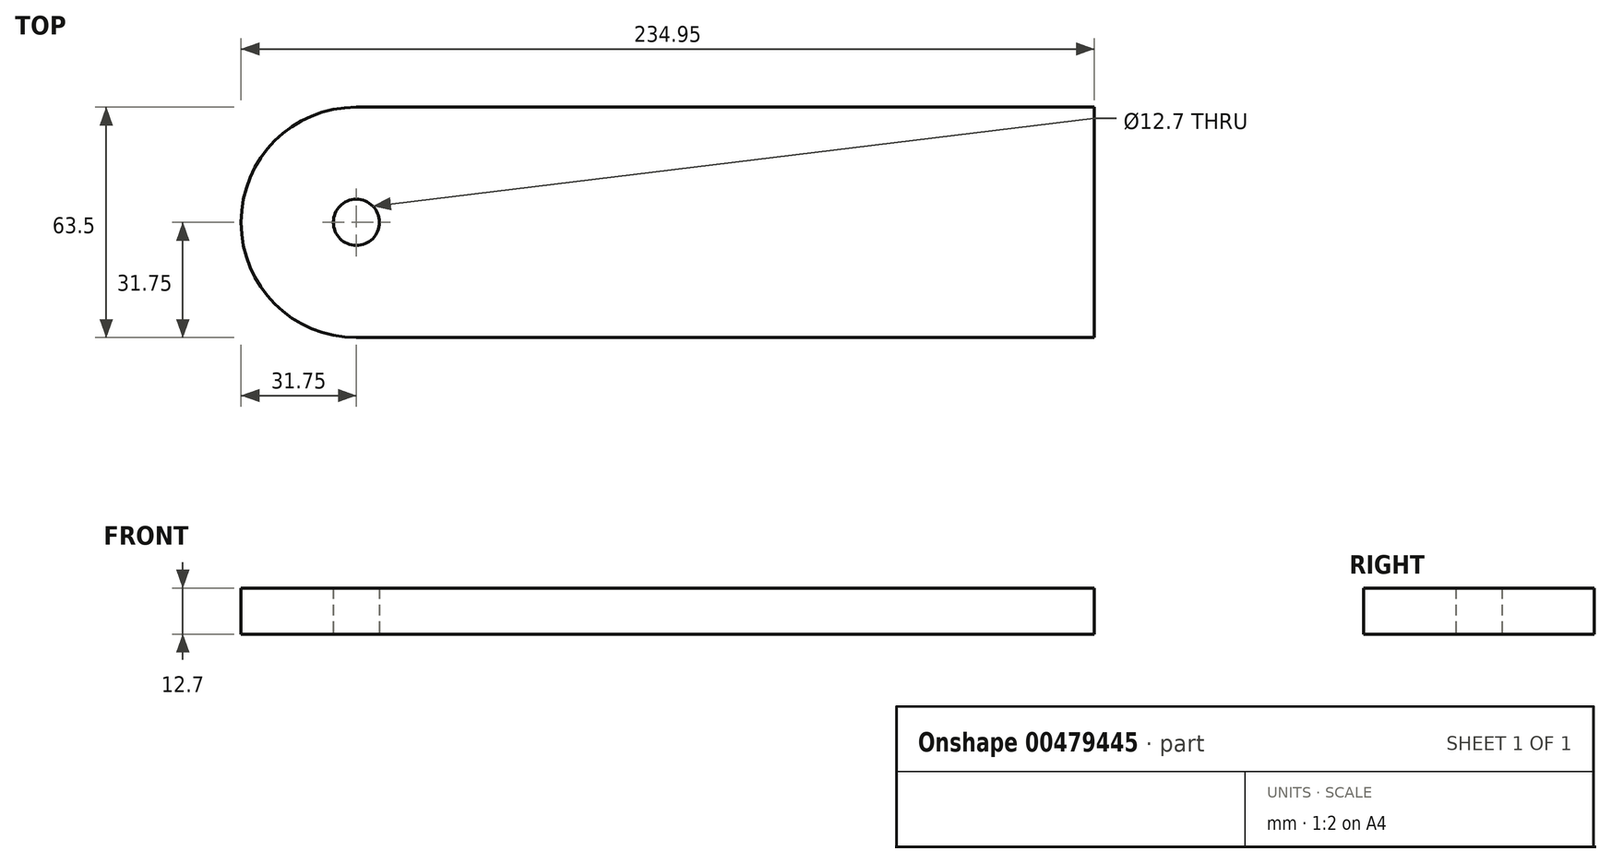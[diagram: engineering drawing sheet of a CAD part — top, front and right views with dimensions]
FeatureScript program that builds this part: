
annotation { "Feature Type Name" : "Feature", "Feature Type Description" : "" }
export const myFeature = defineFeature(function(context is Context, id is Id, definition is map)
    precondition{}
    {
        {
            var Q0;
            Q0=qCreatedBy(makeId("Top.planeOp"),FACE);
            var sketch = newSketch(context, id + "F0", { "sketchPlane" : qUnion([Q0])});
            skCircle(sketch, "E0", {"center": v(0, 0) * mm, "radius": 31.75 * mm});
            skLineSegment(sketch, "E1", {"start": v(203.2, 31.75) * mm, "end": v(203.2, -31.75) * mm});
            skLineSegment(sketch, "E2", {"start": v(203.2, 31.75) * mm, "end": v(0, 31.75) * mm});
            skLineSegment(sketch, "E3", {"start": v(203.2, -31.75) * mm, "end": v(0, -31.75) * mm});
            skCircle(sketch, "E4", {"center": v(0, 0) * mm, "radius": 6.35 * mm});
            skSolve(sketch);
        }
        {
            var Q0;
            Q0=makeQuery(id+"F0.imprint","IMPRINT",FACE,{"disambiguationData":[TD([[makeQuery(id+"F0.imprint","IMPRINT",EDGE,{"derivedFrom":sQuery(id+"F0.wireOp",EDGE,"E1")}),-1.0]])]});
            var Q1;
            Q1=makeQuery(id+"F0.imprint","IMPRINT",FACE,{"disambiguationData":[TD([[makeQuery(id+"F0.imprint","IMPRINT",EDGE,{"derivedFrom":sQuery(id+"F0.wireOp",EDGE,"E4")}),-1.0]])]});
            extrude(context, id + "F1", {"entities" : qUnion([Q0, Q1]), "depth" : 12.7 * mm});
        }
    });
